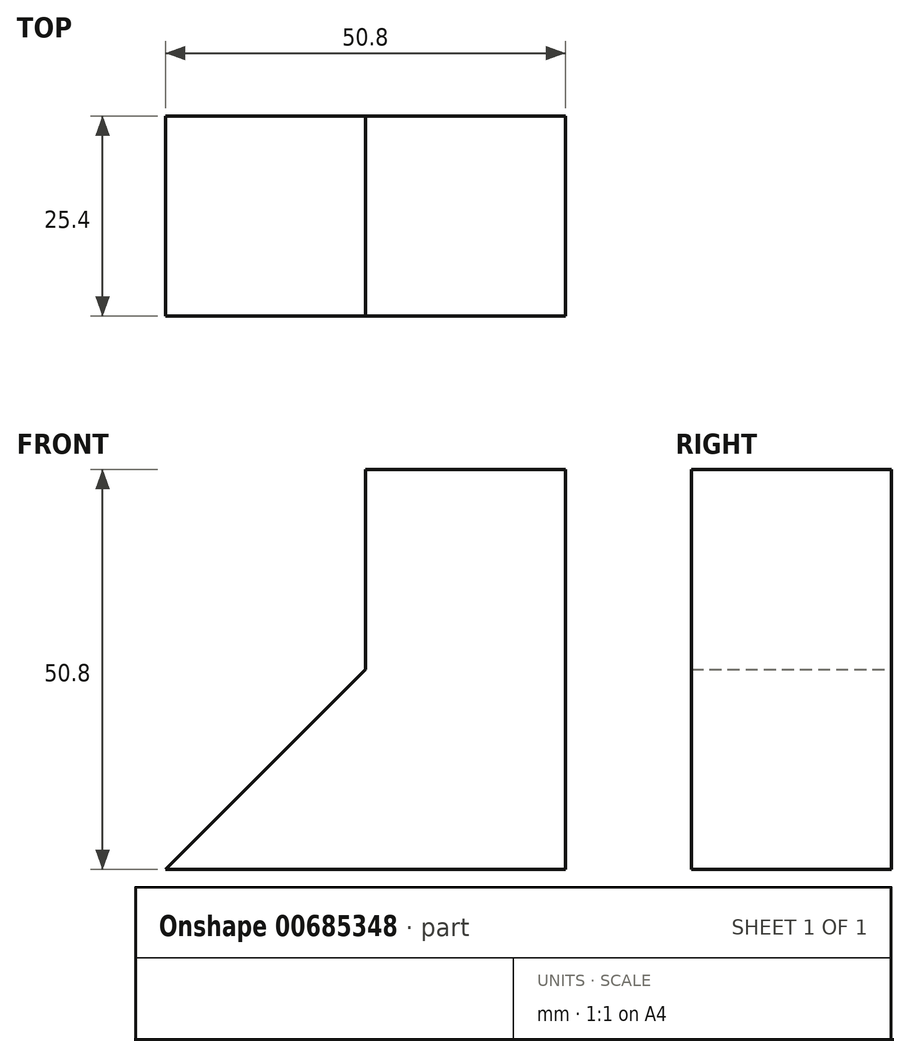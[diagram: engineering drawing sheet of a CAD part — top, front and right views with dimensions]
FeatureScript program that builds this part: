
annotation { "Feature Type Name" : "Feature", "Feature Type Description" : "" }
export const myFeature = defineFeature(function(context is Context, id is Id, definition is map)
    precondition{}
    {
        {
            var Q0;
            Q0=qCreatedBy(makeId("Front.planeOp"),FACE);
            var sketch = newSketch(context, id + "F0", { "sketchPlane" : qUnion([Q0])});
            skLineSegment(sketch, "E0", {"start": v(0, 0) * mm, "end": v(0, 25.4) * mm});
            skLineSegment(sketch, "E1", {"start": v(0, 25.4) * mm, "end": v(25.4, 25.4) * mm});
            skLineSegment(sketch, "E2", {"start": v(25.4, 25.4) * mm, "end": v(25.4, -25.4) * mm});
            skLineSegment(sketch, "E3", {"start": v(25.4, -25.4) * mm, "end": v(-25.4, -25.4) * mm});
            skLineSegment(sketch, "E4", {"start": v(-25.4, -25.4) * mm, "end": v(0, 0) * mm});
            skSolve(sketch);
        }
        {
            var Q0;
            Q0=makeQuery(id+"F0.imprint","IMPRINT",FACE,{"disambiguationData":[TD([[makeQuery(id+"F0.imprint","IMPRINT",EDGE,{"derivedFrom":sQuery(id+"F0.wireOp",EDGE,"E0")}),-1.0]])]});
            extrude(context, id + "F1", {"entities" : qUnion([Q0]), "depth" : 25.4 * mm, "offsetDistance" : 25.4 * mm});
        }
    });
